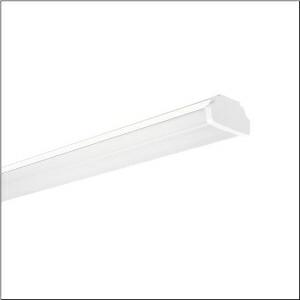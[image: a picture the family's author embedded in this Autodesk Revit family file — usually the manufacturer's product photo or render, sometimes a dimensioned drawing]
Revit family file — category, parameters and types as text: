
# Revit family: modario_r__31_gen_2_53bm812cv475c2_f996
name_source: partatom
category: Lighting Fixtures
units: mm (PartAtom-declared; Revit-internal decimal feet)

## family parameters
Cut with Voids When Loaded = No
Host = Face
Light Source = No
Part Type = Normal
Room Calculation Point = No
Round Connector Dimension = Use Diameter
Shared = No

## types (1)
- --- (1 x LED, 7600 lm, 40.5 W, 4000K)
    Apparent Load = 41 VA
    CIE Flux Codes = 47 80 95 93 100
    Color Rendering = 80
    Color Temperature = 4000K
    Default Elevation = 1800 mm
    Description = Modario® 31 Gen.2, luminaire insert, of sheet steel, coil coated, white, length: 1.495mm, width: 81mm, height: 82mm, 5x system unit, system units: 299mm, LED rated luminous flux: 7.600lm, light colour: 840, control gear: ON/OFF Multilumen, CLOi, with plug, 3-pole, with phase selection, mains connection: 220..240V, AC, 50/60Hz, start of lifetime: 41W, end of service life: 48W, through-wiring accessed according to module size, primary optical cover: cover, of PMMA, light emission: direct distribution, primary light characteristic: symmetric, protection rating (complete): IP20, protection rating (LED compartment): IP50, insulation class (complete): insulation class I (protective earthing), certification: CE, ENEC, VDE, UKCA, impact resistance: IK03, permissible ambient temperature for indoor applications: -35..+50°C, corresponds to IFS (International Featured Standards) requirements for safety and quality in the food industry, reducing of maximum allowable ambient temperature of 5°C with ceiling mounting, IP40 when using the optional accessory 5TP9018, packaging unit: 1 piece
    Height = 92 mm
    Lamp = 1 x LED
    Lamp Light Flux = 7600 lm
    Lamp Power = 40.5 W
    Lamp count = 1
    Length = 1495 mm
    Luminous efficacy = 188 lm/W
    Manufacturer = Siteco
    ModVariant = No
    Model = 53BM812CV475C2
    Mounting Place = Ceiling
    Mounting Type = Pendant
    Number of Poles = 1
    OnlyDefault = Yes
    Power Factor = 1
    Product Name = Modario® 31 Gen.2
    Product group = luminaire insert
    ProductGroupID = 902
    Protection Class = Protection class I
    Protection Degree = IP 20
    RLX_Detail_Level = 1
    RLX_Emergency_Light_Flux = 0 lm
    RLX_Emergency_Type = 0
    RLX_Emergency_Type_DB = No
    RlxData = <blob elided: 40085 chars, md5=557adc1a>
    Socket = socket
    Standby Power = 0 W
    System Light Flux = 7600 lm
    System Power = 41 W
    Type Comments = factory setting: luminous flux: 100 % | (A | C | E) | 94 mA
    Type Image = l_1341886.jpg
    URL = http://relux.com
    VarID = @adj_034114
    Voltage = 0 V
    Weight = 0.00 kg
    Width = 81 mm

## geometry (parser evidence)
native form markers: Blend x4, Sweep x12
no freeform markers — native parametric forms only
